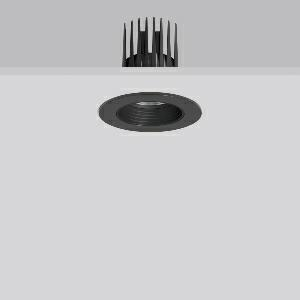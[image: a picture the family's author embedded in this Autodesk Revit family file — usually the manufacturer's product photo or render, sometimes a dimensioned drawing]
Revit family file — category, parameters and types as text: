
# Revit family: heledon_mini_e_901752_003_2_76_3fb4
name_source: partatom
category: Lighting Fixtures
units: mm (PartAtom-declared; Revit-internal decimal feet)

## family parameters
Cut with Voids When Loaded = No
Host = Face
Light Source = No
Part Type = Normal
Room Calculation Point = No
Round Connector Dimension = Use Diameter
Shared = No

## types (1)
- HELEDON mini E (1 x LED Modul 927, 2850 lm, 2700)
    Apparent Load = 29 VA
    Approval mark = CE
    CIE Flux Codes = 96 100 100 100 100
    Color Rendering = 92
    Color Temperature = 2700
    Default Elevation = 1800 mm
    Description = Series: HELEDON mini
Round recessed downlight. Housing: die-cast aluminium, powder-coated. Black plastic ring and recessed LED to prevent glare from the side. Optical assembly with lens made of plastic (polycarbonate) for the best homogeneous light distribution - can be changed without tools. Best colour rendering index Ra>90. Suitable for Recessed ceiling mounting. Installation without tools thanks to spring fastening system. Including separate LED converter with connecting cable 600 mm.High quality converter without flickering and stroboscopic effect. Through-wiring box (5 pole) available as accessory. The following accessories can be mounted without use of tools: interchangeable lenses, decorative glasses, honeycomb louvre, clear and frosted diffusers, white interchangeable plastic ring. 
Colour: deep black, matt (RAL 9005)
Diameter: 124 mm
Height: 3 mm
Cut-out diameter: 114 mm
Recess height: 170 mm
Luminaire: recess height: 120 mm
Lamp: LED
Socket: without socket
Colour temperature: 2700K
Colour rendering index (CRI): 92
System power: 29 W
Rated luminous flux: 2850 lm
Luminous efficiency: 98 lm/W
Control gear: Converter, dimmable, DALI
Protection class: II
Type of protection: IP 20
    Height = 0 mm  [stored 0 ft]
    Lamp = 1 x LED Modul 927
    Lamp Light Flux = 2850 lm
    Lamp count = 1
    Length = 124 mm  [stored 0.406824 ft]
    Lifetime = 50000 h
    Luminous efficacy = 98 lm/W
    Manufacturer = RZB
    ModVariant = No
    Model = 901752.003.2.76
    Mounting Place = Ceiling
    Mounting Type = Recessed
    Number of Poles = 1
    OnlyDefault = Yes
    Power Factor = 1
    Product Name = HELEDON mini E
    Product group = Recessed downlights
    ProductGroupID = 402
    Protection Class = Protection class II
    Protection Degree = IP 20
    RLX_Detail_Level = 1
    RLX_Emergency_Light_Flux = 0 lm
    RLX_Emergency_Type = 0
    RLX_Emergency_Type_DB = No
    RlxData = <blob elided: 125301 chars, md5=b23ba262>
    Socket = socket
    Standby Power = 0 W
    System Light Flux = 2850 lm
    System Power = 29 W
    Type Comments = Product without accessories
    Type Image = 901656.003.jpg
    URL = http://relux.com
    VarID = ---
    Voltage = 230 V
    Voltage Range = 220-240 V
    Weight = 0.00 kg
    Width = 0 mm  [stored 0 ft]

note: [stored X ft] marks values corroborated as IEEE doubles in the binary element streams (Revit-internal decimal feet)

## geometry (parser evidence)
native form markers: Blend x4, Sweep x12
no freeform markers — native parametric forms only
